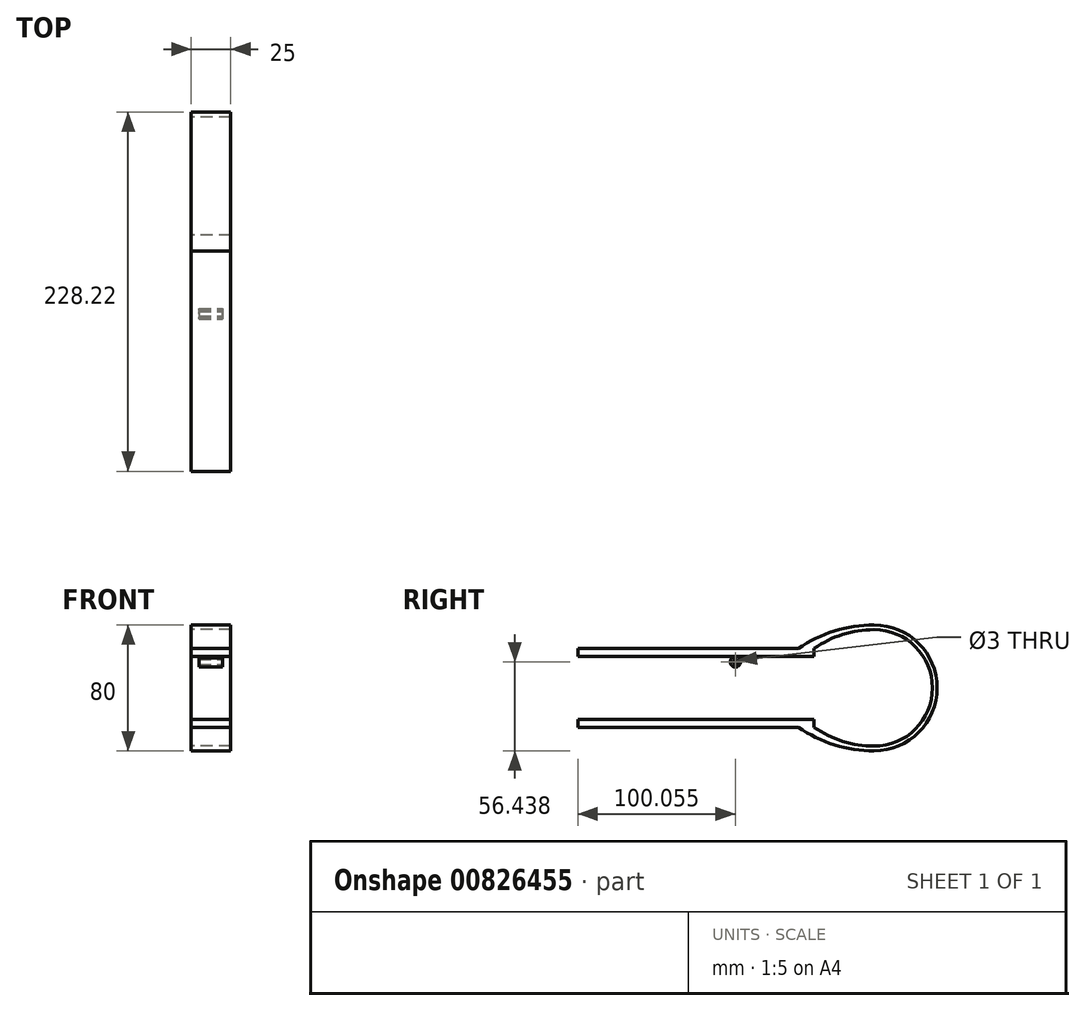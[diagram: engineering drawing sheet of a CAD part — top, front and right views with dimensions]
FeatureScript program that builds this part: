
annotation { "Feature Type Name" : "Feature", "Feature Type Description" : "" }
export const myFeature = defineFeature(function(context is Context, id is Id, definition is map)
    precondition{}
    {
        {
            var Q0;
            Q0=qCreatedBy(makeId("Right.planeOp"),FACE);
            var sketch = newSketch(context, id + "F0", { "sketchPlane" : qUnion([Q0])});
            skArc(sketch, "E0", {"start": v(0, -40) * mm, "mid": v(40, 0) * mm, "end": v(0, 40) * mm});
            skArc(sketch, "E1", {"start": v(0, -37) * mm, "mid": v(37, 0) * mm, "end": v(0, 37) * mm});
            skArc(sketch, "E2", {"start": v(0, 40) * mm, "mid": v(-25.25, 36.16) * mm, "end": v(-48.22, 25) * mm});
            skArc(sketch, "E3", {"start": v(-48.22, -25) * mm, "mid": v(-25.25, -36.16) * mm, "end": v(0, -40) * mm});
            skArc(sketch, "E4", {"start": v(-38.22, -25) * mm, "mid": v(-20.03, -33.93) * mm, "end": v(0, -37) * mm});
            skArc(sketch, "E5", {"start": v(0, 37) * mm, "mid": v(-20.03, 33.93) * mm, "end": v(-38.22, 25) * mm});
            skLineSegment(sketch, "E6", {"start": v(-38.22, 25) * mm, "end": v(-38.22, 20) * mm});
            skLineSegment(sketch, "E7", {"start": v(-38.22, 20) * mm, "end": v(-188.22, 20) * mm});
            skLineSegment(sketch, "E8", {"start": v(-188.22, 20) * mm, "end": v(-188.22, 25) * mm});
            skLineSegment(sketch, "E9", {"start": v(-188.22, 25) * mm, "end": v(-48.22, 25) * mm});
            skLineSegment(sketch, "E10", {"start": v(-38.22, -25) * mm, "end": v(-38.22, -20) * mm});
            skLineSegment(sketch, "E11", {"start": v(-38.22, -20) * mm, "end": v(-188.22, -20) * mm});
            skLineSegment(sketch, "E12", {"start": v(-188.22, -20) * mm, "end": v(-188.22, -25) * mm});
            skLineSegment(sketch, "E13", {"start": v(-188.22, -25) * mm, "end": v(-48.22, -25) * mm});
            skSolve(sketch);
        }
        {
            var Q0;
            Q0 = qSketchRegion(id + "F0", true);
            extrude(context, id + "F1", {"entities" : qUnion([Q0]), "depth" : 25 * mm, "offsetDistance" : 25 * mm});
        }
        {
            var Q0;
            Q0=makeQuery(id+"F1.opExtrude","SWEPT_FACE",FACE,{"disambiguationData":[OSD([sQuery(id+"F0.wireOp",EDGE,"E7")])]});
            var sketch = newSketch(context, id + "F2", { "sketchPlane" : qUnion([Q0])});
            skPoint(sketch, "E14", {"position": v(25, 88.22) * mm});
            skLineSegment(sketch, "E15.bottom", {"start": v(5, 80.72) * mm, "end": v(20, 80.72) * mm});
            skLineSegment(sketch, "E15.top", {"start": v(5, 95.72) * mm, "end": v(20, 95.72) * mm});
            skLineSegment(sketch, "E15.left", {"start": v(5, 80.72) * mm, "end": v(5, 95.72) * mm});
            skLineSegment(sketch, "E15.right", {"start": v(20, 80.72) * mm, "end": v(20, 95.72) * mm});
            skPoint(sketch, "E15.middle", {"position": v(12.5, 88.22) * mm});
            skPoint(sketch, "E16", {"position": v(12.5, 188.22) * mm});
            skSolve(sketch);
        }
        {
            var Q0;
            Q0 = qSketchRegion(id + "F2", true);
            extrude(context, id + "F3", {"entities" : qUnion([Q0]), "operationType" : NewBodyOperationType.ADD, "depth" : 10 * mm, "offsetDistance" : 25 * mm});
        }
        {
            var Q0;
            Q0=makeQuery(id+"F3.opExtrude","SWEPT_FACE",FACE,{"disambiguationData":[OSD([sQuery(id+"F2.wireOp",EDGE,"E15.right")])]});
            var sketch = newSketch(context, id + "F4", { "sketchPlane" : qUnion([Q0])});
            skLineSegment(sketch, "E17", {"start": v(-90.17, 20) * mm, "end": v(-90.17, 19) * mm});
            skLineSegment(sketch, "E18", {"start": v(-86.17, 20) * mm, "end": v(-86.17, 19) * mm});
            skArc(sketch, "E19", {"start": v(-90.17, 19) * mm, "mid": v(-88.17, 13.19) * mm, "end": v(-86.17, 19) * mm});
            skLineSegment(sketch, "E20", {"start": v(-90.17, 20) * mm, "end": v(-95.72, 20) * mm});
            skLineSegment(sketch, "E21", {"start": v(-95.72, 20) * mm, "end": v(-95.72, 10) * mm});
            skLineSegment(sketch, "E22", {"start": v(-95.72, 10) * mm, "end": v(-80.72, 10) * mm});
            skLineSegment(sketch, "E23", {"start": v(-80.72, 10) * mm, "end": v(-80.72, 20) * mm});
            skLineSegment(sketch, "E24", {"start": v(-80.72, 20) * mm, "end": v(-86.17, 20) * mm});
            skCircle(sketch, "E25", {"center": v(-88.17, 16.44) * mm, "radius": 1.5 * mm});
            skSolve(sketch);
        }
        {
            var Q0;
            Q0 = qSketchRegion(id + "F4", true);
            extrude(context, id + "F5", {"entities" : qUnion([Q0]), "operationType" : NewBodyOperationType.REMOVE, "oppositeDirection" : true, "depth" : 25 * mm, "offsetDistance" : 25 * mm});
        }
    });
